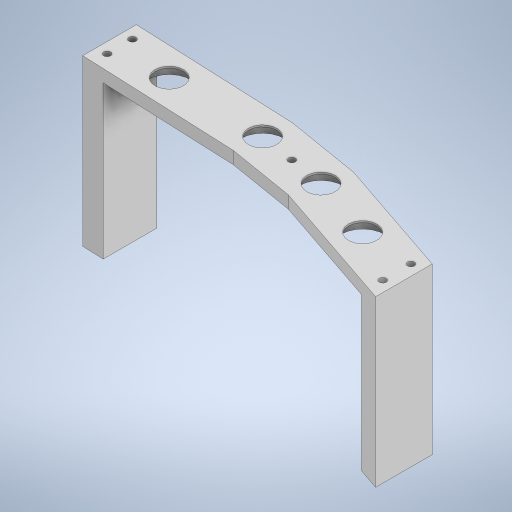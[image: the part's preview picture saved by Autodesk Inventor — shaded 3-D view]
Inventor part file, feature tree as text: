
AUTODESK INVENTOR PART (.ipt)
format: ipt  version: 2023 (Build 270158000, 158)  size: 323,584 bytes
history: native  units: mm
features: extrude x4
ambient origin geometry x8: Origin, YZ Plane, XZ Plane, XY Plane, X Axis, Y Axis, Z Axis, Center Point
bodies: Solid1 (feature_tree)
feature tree (4):
  extrude  "Extrusion1"  Depth=3.0mm TaperAngle=0.0deg
  extrude  "Extrusion2"  Depth=0.5mm TaperAngle=0.0deg
  extrude  "Extrusion8"  Depth=46.0mm TaperAngle=0.0deg
  extrude  "Extrusion9"  TaperAngle=0.0deg  [1 undecoded]
note: 1 required parameter value undecoded (feature->parameter linkage not recoverable at this tier; creation-order binding heuristic only, values carry confidence <= 0.55)
